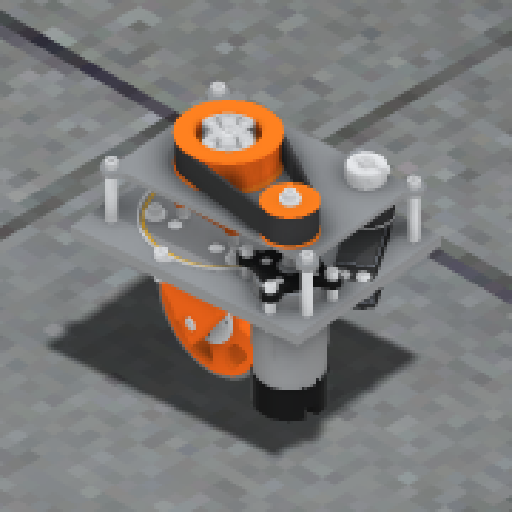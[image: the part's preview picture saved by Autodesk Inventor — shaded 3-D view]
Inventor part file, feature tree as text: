
AUTODESK INVENTOR PART (.ipt)
format: ipt  version: 2024.2 (Build 282272000, 272)  size: 62,776,832 bytes
history: native  units: in
note: dims shown in document units (in); Inventor stores cm internally (conversion verified against a paired STEP export)
features: other x3, plane x1
ambient origin geometry x8: Origin, YZ Plane, XZ Plane, XY Plane, X Axis, Y Axis, Z Axis, Center Point
bodies: Solid1 (feature_tree)
feature tree (4):
  other  "Pod_pre_mirror.ipt"
  other  "Solid1::Pod_pre_mirror.ipt"
  other  "TaggingFeature1"
  plane  "Work Plane2_1"
